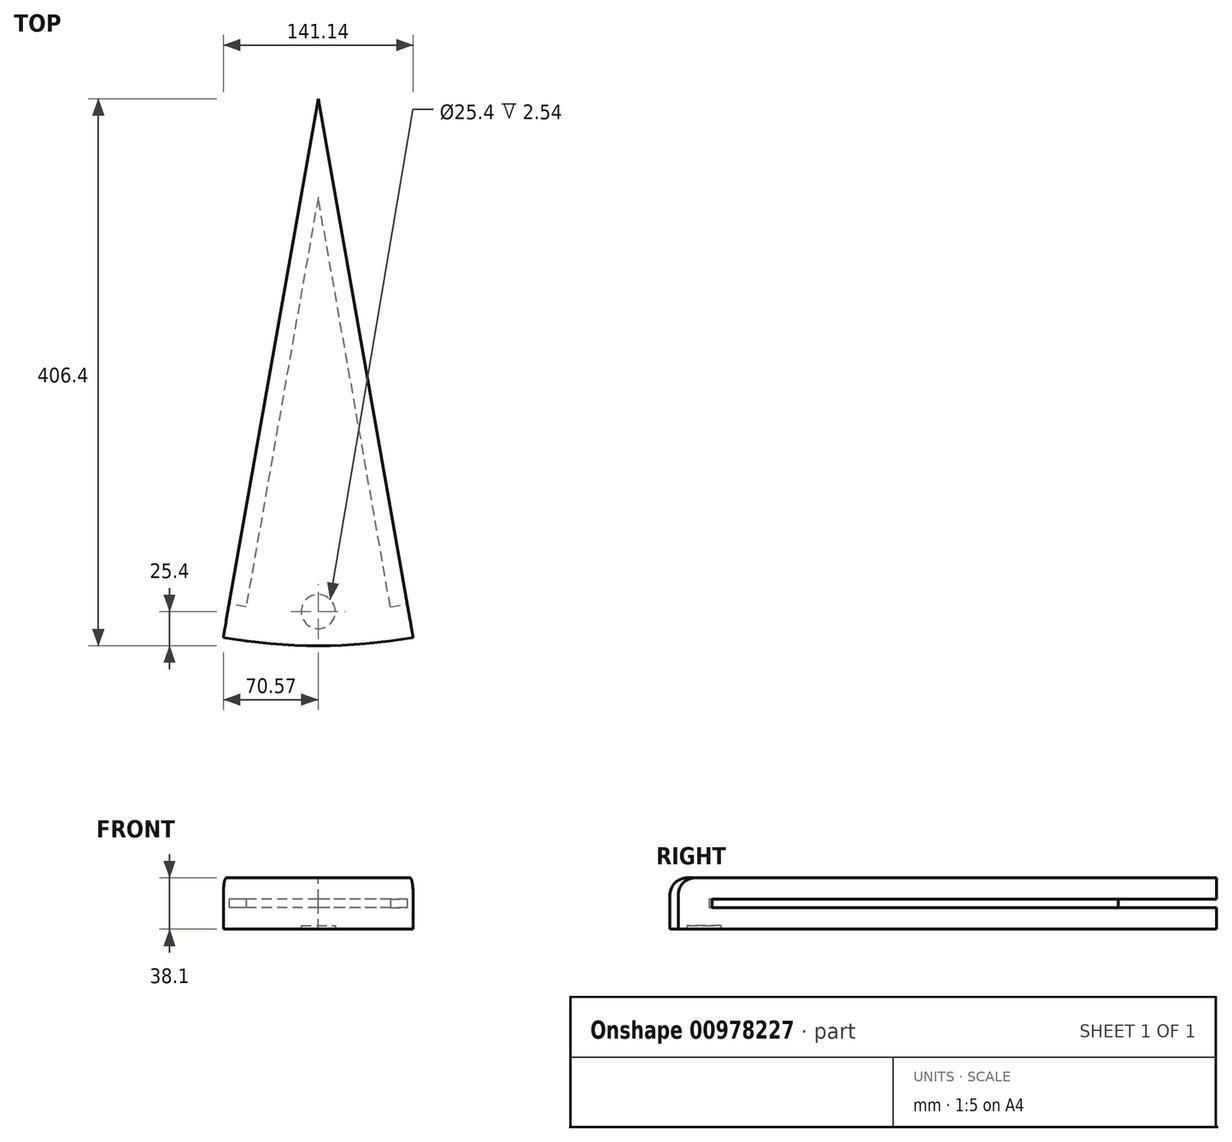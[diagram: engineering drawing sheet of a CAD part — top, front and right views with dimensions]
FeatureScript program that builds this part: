
annotation { "Feature Type Name" : "Feature", "Feature Type Description" : "" }
export const myFeature = defineFeature(function(context is Context, id is Id, definition is map)
    precondition{}
    {
        {
            var Q0;
            Q0=qCreatedBy(makeId("Top.planeOp"),FACE);
            var sketch = newSketch(context, id + "F0", { "sketchPlane" : qUnion([Q0])});
            skArc(sketch, "E0", {"start": v(-70.57, -400.23) * mm, "mid": v(0, -406.4) * mm, "end": v(70.57, -400.23) * mm});
            skLineSegment(sketch, "E1", {"start": v(0, 0) * mm, "end": v(-70.57, -400.23) * mm});
            skLineSegment(sketch, "E2", {"start": v(0, 0) * mm, "end": v(70.57, -400.23) * mm});
            skLineSegment(sketch, "E3", {"start": v(0, 0) * mm, "end": v(0, -406.4) * mm, "construction": true});
            skSolve(sketch);
        }
        {
            var Q0;
            Q0=makeQuery(id+"F0.imprint","IMPRINT",FACE,{"disambiguationData":[TD([[makeQuery(id+"F0.imprint","IMPRINT",EDGE,{"derivedFrom":sQuery(id+"F0.wireOp",EDGE,"E0")}),1.0]])]});
            extrude(context, id + "F1", {"entities" : qUnion([Q0]), "oppositeDirection" : true, "depth" : 38.1 * mm, "offsetDistance" : 25.4 * mm});
        }
        {
            var Q0;
            Q0=makeQuery(id+"F1.opExtrude","CAP_EDGE",EDGE,{"disambiguationData":[OSD([sQuery(id+"F0.wireOp",EDGE,"E0")])],"isStart":true});
            fillet(context, id + "F2", {"entities" : qUnion([Q0]), "radius" : 12.7 * mm, "tangentPropagation" : true, "allowEdgeOverflow" : false});
        }
        {
            var Q0;
            Q0=makeQuery(id+"F1.opExtrude","SWEPT_FACE",FACE,{"disambiguationData":[OSD([sQuery(id+"F0.wireOp",EDGE,"E2")])]});
            var sketch = newSketch(context, id + "F3", { "sketchPlane" : qUnion([Q0])});
            skLineSegment(sketch, "E4.bottom", {"start": v(-381, -15.88) * mm, "end": v(0, -15.88) * mm});
            skLineSegment(sketch, "E4.top", {"start": v(-381, -22.23) * mm, "end": v(0, -22.23) * mm});
            skLineSegment(sketch, "E4.left", {"start": v(-381, -15.88) * mm, "end": v(-381, -22.23) * mm});
            skLineSegment(sketch, "E4.right", {"start": v(0, -15.88) * mm, "end": v(0, -22.23) * mm});
            skLineSegment(sketch, "E5", {"start": v(0, -19.05) * mm, "end": v(-381, -19.05) * mm, "construction": true});
            skSolve(sketch);
        }
        {
            var Q0;
            Q0=makeQuery(id+"F3.imprint","IMPRINT",FACE,{"disambiguationData":[TD([[makeQuery(id+"F3.imprint","IMPRINT",EDGE,{"derivedFrom":sQuery(id+"F3.wireOp",EDGE,"E4.bottom")}),-1.0]])]});
            extrude(context, id + "F4", {"entities" : qUnion([Q0]), "operationType" : NewBodyOperationType.REMOVE, "oppositeDirection" : true, "depth" : 12.7 * mm, "offsetDistance" : 25.4 * mm});
        }
        {
            var Q0;
            Q0=makeQuery(id+"F1.opExtrude","SWEPT_FACE",FACE,{"disambiguationData":[OSD([sQuery(id+"F0.wireOp",EDGE,"E1")])]});
            var sketch = newSketch(context, id + "F5", { "sketchPlane" : qUnion([Q0])});
            skLineSegment(sketch, "E6.bottom", {"start": v(37.13, -15.88) * mm, "end": v(381, -15.87) * mm});
            skLineSegment(sketch, "E6.top", {"start": v(37.13, -22.23) * mm, "end": v(381, -22.22) * mm});
            skLineSegment(sketch, "E6.left", {"start": v(37.13, -15.88) * mm, "end": v(37.13, -22.23) * mm});
            skLineSegment(sketch, "E6.right", {"start": v(381, -15.87) * mm, "end": v(381, -22.22) * mm});
            skSolve(sketch);
        }
        {
            var Q0;
            Q0=makeQuery(id+"F5.imprint","IMPRINT",FACE,{"disambiguationData":[TD([[makeQuery(id+"F5.imprint","IMPRINT",EDGE,{"derivedFrom":sQuery(id+"F5.wireOp",EDGE,"E6.bottom")}),-1.0]])]});
            extrude(context, id + "F6", {"entities" : qUnion([Q0]), "operationType" : NewBodyOperationType.REMOVE, "oppositeDirection" : true, "depth" : 12.7 * mm, "offsetDistance" : 25.4 * mm});
        }
        {
            var Q0;
            Q0=makeQuery(id+"F1.opExtrude","CAP_FACE",FACE,{"disambiguationData":[OSD([sQuery(id+"F0.wireOp",EDGE,"E0"),sQuery(id+"F0.wireOp",EDGE,"E1"),sQuery(id+"F0.wireOp",EDGE,"E2")])],"isStart":false});
            var sketch = newSketch(context, id + "F7", { "sketchPlane" : qUnion([Q0])});
            skCircle(sketch, "E7", {"center": v(0, 381) * mm, "radius": 12.7 * mm});
            skSolve(sketch);
        }
        {
            var Q0;
            Q0 = qSketchRegion(id + "F7", true);
            extrude(context, id + "F8", {"entities" : qUnion([Q0]), "operationType" : NewBodyOperationType.REMOVE, "oppositeDirection" : true, "depth" : 2.54 * mm, "offsetDistance" : 25.4 * mm});
        }
    });
